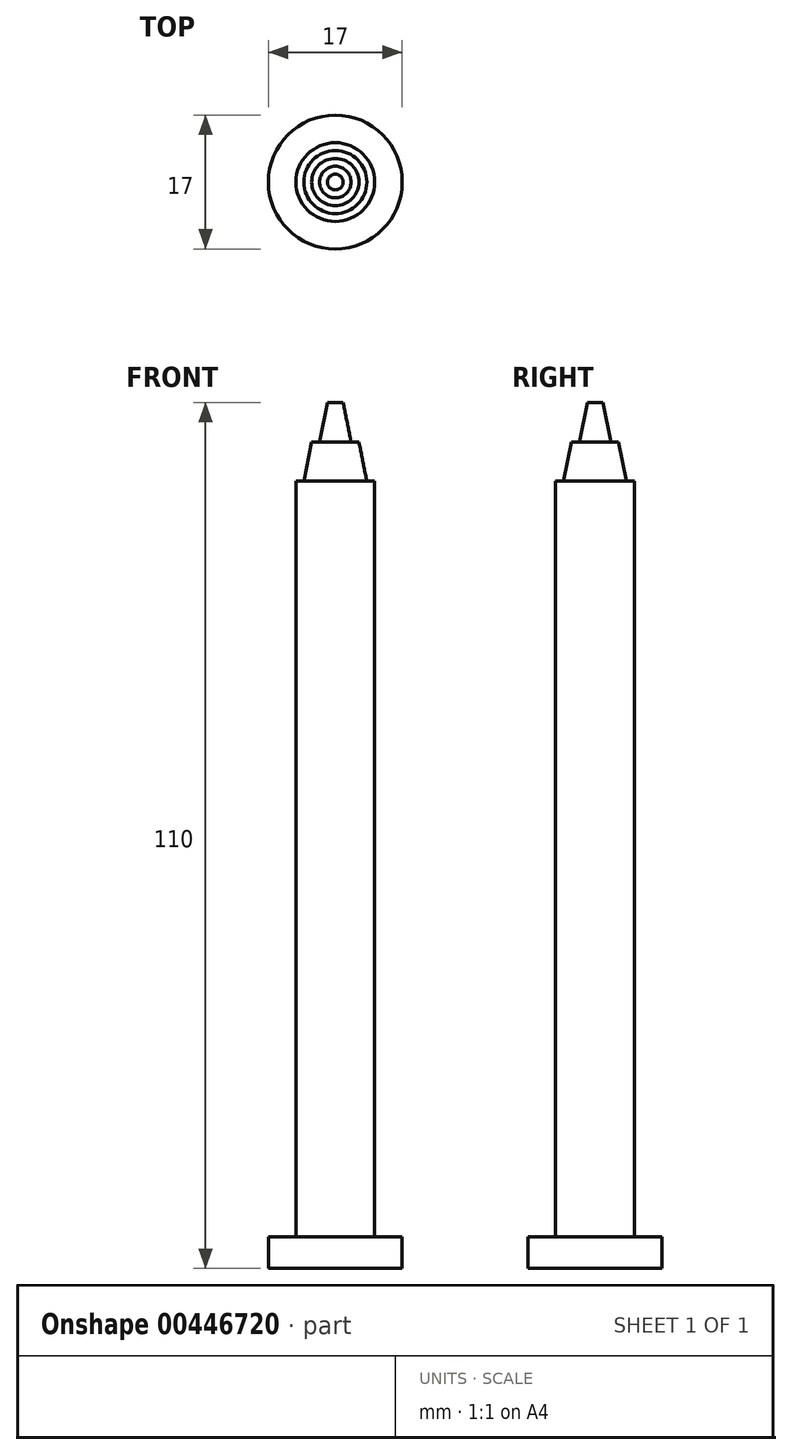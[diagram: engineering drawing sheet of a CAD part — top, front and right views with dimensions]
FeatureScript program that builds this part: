
annotation { "Feature Type Name" : "Feature", "Feature Type Description" : "" }
export const myFeature = defineFeature(function(context is Context, id is Id, definition is map)
    precondition{}
    {
        {
            var Q0;
            Q0=qCreatedBy(makeId("Top.planeOp"),FACE);
            var sketch = newSketch(context, id + "F0", { "sketchPlane" : qUnion([Q0])});
            skCircle(sketch, "E0", {"center": v(0, 0) * mm, "radius": 8.5 * mm});
            skSolve(sketch);
        }
        {
            var Q0;
            Q0=qSketchRegion(id+"F0",true);
            extrude(context, id + "F1", {"entities" : qUnion([Q0]), "depth" : 4 * mm});
        }
        {
            var Q0;
            Q0=qCreatedBy(makeId("Top.planeOp"),FACE);
            var sketch = newSketch(context, id + "F2", { "sketchPlane" : qUnion([Q0])});
            skCircle(sketch, "E1", {"center": v(0, 0) * mm, "radius": 5 * mm});
            skSolve(sketch);
        }
        {
            var Q0;
            Q0=qSketchRegion(id+"F2",true);
            extrude(context, id + "F3", {"entities" : qUnion([Q0]), "operationType" : NewBodyOperationType.ADD, "depth" : 100 * mm});
        }
        {
            var Q0;
            Q0=qCreatedBy(makeId("Right.planeOp"),FACE);
            var sketch = newSketch(context, id + "F4", { "sketchPlane" : qUnion([Q0])});
            skLineSegment(sketch, "E2", {"start": v(0, 105) * mm, "end": v(0, 100) * mm});
            skLineSegment(sketch, "E3", {"start": v(0, 100) * mm, "end": v(4, 100) * mm});
            skLineSegment(sketch, "E4", {"start": v(4, 100) * mm, "end": v(3, 105) * mm});
            skLineSegment(sketch, "E5", {"start": v(3, 105) * mm, "end": v(0, 105) * mm});
            skSolve(sketch);
        }
        {
            var Q0;
            Q0=makeQuery(id+"F4.imprint","IMPRINT",FACE,{"disambiguationData":[TD([[makeQuery(id+"F4.imprint","IMPRINT",EDGE,{"derivedFrom":sQuery(id+"F4.wireOp",EDGE,"E2")}),1.0]])]});
            var Q1;
            Q1=sQuery(id+"F4.wireOp",EDGE,"E2");
            revolve(context, id + "F5", {"operationType" : NewBodyOperationType.ADD, "entities" : qUnion([Q0]), "axis" : qUnion([Q1]), "revolveType" : RevolveType.FULL});
        }
        {
            var Q0;
            Q0=qCreatedBy(makeId("Right.planeOp"),FACE);
            var sketch = newSketch(context, id + "F6", { "sketchPlane" : qUnion([Q0])});
            skLineSegment(sketch, "E6", {"start": v(0, 110) * mm, "end": v(0, 105) * mm});
            skLineSegment(sketch, "E7", {"start": v(0, 105) * mm, "end": v(2, 105) * mm});
            skLineSegment(sketch, "E8", {"start": v(2, 105) * mm, "end": v(1, 110) * mm});
            skLineSegment(sketch, "E9", {"start": v(1, 110) * mm, "end": v(0, 110) * mm});
            skSolve(sketch);
        }
        {
            var Q0;
            Q0=makeQuery(id+"F6.imprint","IMPRINT",FACE,{"disambiguationData":[TD([[makeQuery(id+"F6.imprint","IMPRINT",EDGE,{"derivedFrom":sQuery(id+"F6.wireOp",EDGE,"E6")}),1.0]])]});
            var Q1;
            Q1=sQuery(id+"F6.wireOp",EDGE,"E6");
            revolve(context, id + "F7", {"operationType" : NewBodyOperationType.ADD, "entities" : qUnion([Q0]), "axis" : qUnion([Q1]), "revolveType" : RevolveType.FULL});
        }
    });
